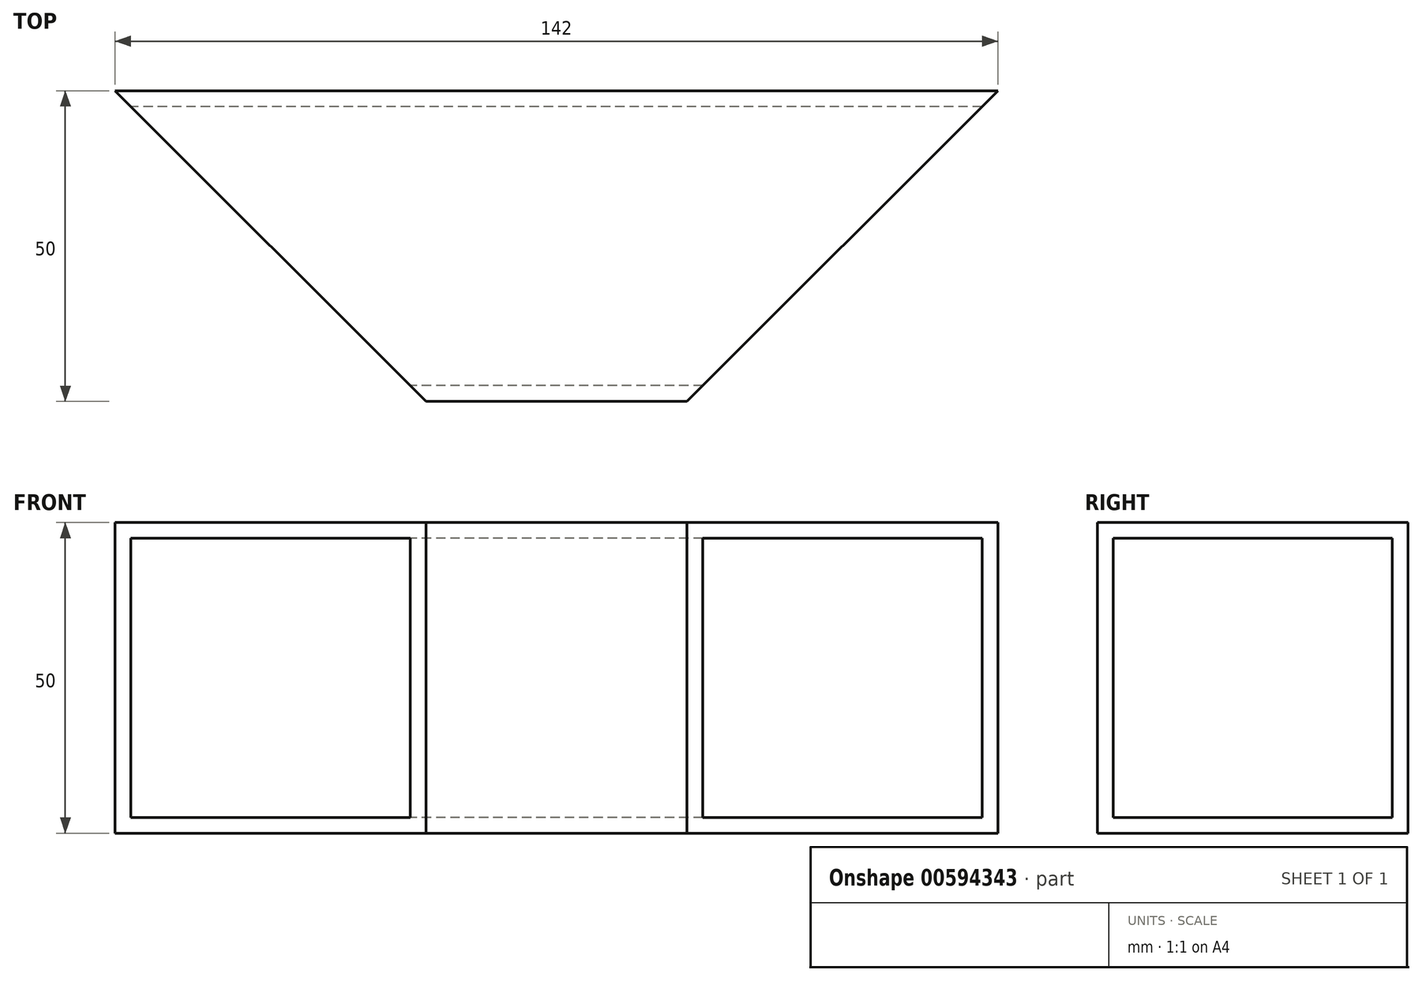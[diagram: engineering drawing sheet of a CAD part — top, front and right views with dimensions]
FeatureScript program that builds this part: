
annotation { "Feature Type Name" : "Feature", "Feature Type Description" : "" }
export const myFeature = defineFeature(function(context is Context, id is Id, definition is map)
    precondition{}
    {
        {
            var Q0;
            Q0=qCreatedBy(makeId("Top.planeOp"),FACE);
            var sketch = newSketch(context, id + "F0", { "sketchPlane" : qUnion([Q0])});
            skLineSegment(sketch, "E0.bottom", {"start": v(-8, -30.56) * mm, "end": v(-50, -30.56) * mm});
            skLineSegment(sketch, "E0.top", {"start": v(-8, 19.44) * mm, "end": v(-50, 19.44) * mm});
            skLineSegment(sketch, "E0.left", {"start": v(-8, -30.56) * mm, "end": v(-8, 19.44) * mm});
            skLineSegment(sketch, "E0.right", {"start": v(-50, -30.56) * mm, "end": v(-50, 19.44) * mm});
            skPoint(sketch, "E0.middle", {"position": v(-29, -5.56) * mm});
            skLineSegment(sketch, "E1", {"start": v(-8, -30.56) * mm, "end": v(42, 19.44) * mm});
            skLineSegment(sketch, "E2", {"start": v(42, 19.44) * mm, "end": v(-8, 19.44) * mm});
            skLineSegment(sketch, "E3", {"start": v(-50, 19.44) * mm, "end": v(-100, 19.44) * mm});
            skLineSegment(sketch, "E4", {"start": v(-100, 19.44) * mm, "end": v(-50, -30.56) * mm});
            skSolve(sketch);
        }
        {
            var Q0;
            Q0=makeQuery(id+"F0.imprint","IMPRINT",FACE,{"disambiguationData":[TD([[makeQuery(id+"F0.imprint","IMPRINT",EDGE,{"derivedFrom":sQuery(id+"F0.wireOp",EDGE,"E0.right")}),1.0]])]});
            var Q1;
            Q1=makeQuery(id+"F0.imprint","IMPRINT",FACE,{"disambiguationData":[TD([[makeQuery(id+"F0.imprint","IMPRINT",EDGE,{"derivedFrom":sQuery(id+"F0.wireOp",EDGE,"E0.bottom")}),-1.0]])]});
            var Q2;
            Q2=makeQuery(id+"F0.imprint","IMPRINT",FACE,{"disambiguationData":[TD([[makeQuery(id+"F0.imprint","IMPRINT",EDGE,{"derivedFrom":sQuery(id+"F0.wireOp",EDGE,"E0.left")}),-1.0]])]});
            extrude(context, id + "F1", {"entities" : qUnion([Q0, Q1, Q2]), "depth" : 50 * mm, "offsetDistance" : 25.4 * mm});
        }
        {
            var Q0;
            Q0=makeQuery(id+"F1.opExtrude","SWEPT_FACE",FACE,{"disambiguationData":[OSD([sQuery(id+"F0.wireOp",EDGE,"E1")])]});
            var Q1;
            Q1=makeQuery(id+"F1.opExtrude","SWEPT_FACE",FACE,{"disambiguationData":[OSD([sQuery(id+"F0.wireOp",EDGE,"E4")])]});
            shell(context, id + "F2", {"entities" : qUnion([Q0, Q1]), "thickness" : 2.54 * mm});
        }
    });
